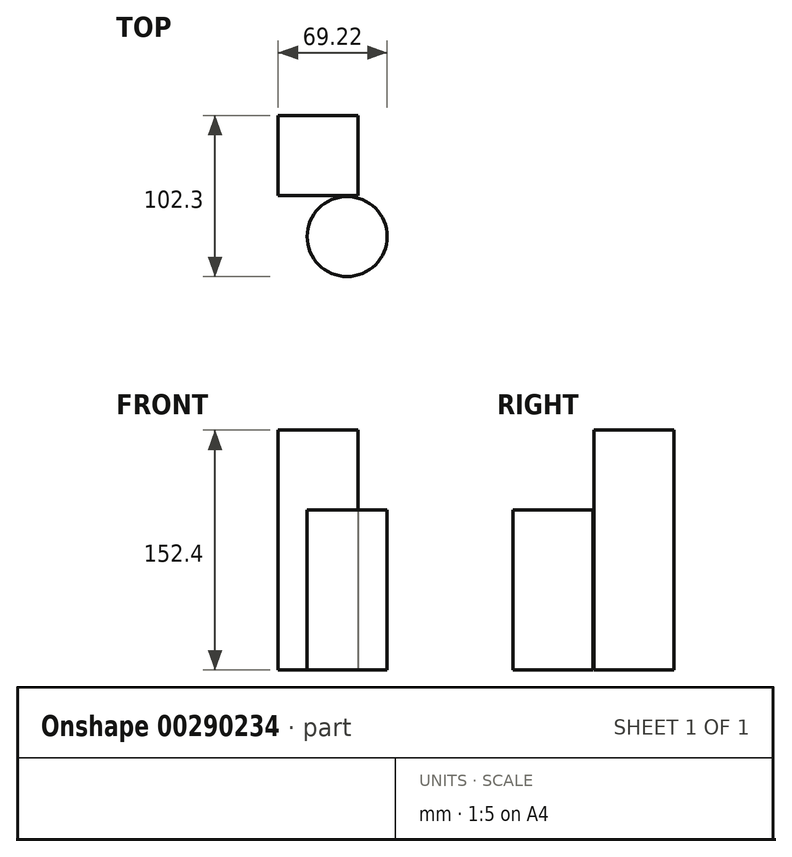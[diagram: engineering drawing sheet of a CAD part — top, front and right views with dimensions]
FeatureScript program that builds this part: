
annotation { "Feature Type Name" : "Feature", "Feature Type Description" : "" }
export const myFeature = defineFeature(function(context is Context, id is Id, definition is map)
    precondition{}
    {
        {
            var Q0;
            Q0=qCreatedBy(makeId("Top.planeOp"),FACE);
            var sketch = newSketch(context, id + "F0", { "sketchPlane" : qUnion([Q0])});
            skCircle(sketch, "E0", {"center": v(0, 0) * mm, "radius": 25.4 * mm});
            skSolve(sketch);
        }
        {
            var Q0;
            Q0=makeQuery(id+"F0.imprint","IMPRINT",FACE,{"disambiguationData":[TD([[makeQuery(id+"F0.imprint","IMPRINT",EDGE,{"derivedFrom":sQuery(id+"F0.wireOp",EDGE,"E0")}),1.0]])]});
            extrude(context, id + "F1", {"entities" : qUnion([Q0]), "depth" : 101.6 * mm});
        }
        {
            var Q0;
            Q0=qCreatedBy(makeId("Top.planeOp"),FACE);
            var sketch = newSketch(context, id + "F2", { "sketchPlane" : qUnion([Q0])});
            skLineSegment(sketch, "E1.bottom", {"start": v(6.98, 76.9) * mm, "end": v(-43.82, 76.9) * mm});
            skLineSegment(sketch, "E1.top", {"start": v(6.98, 26.1) * mm, "end": v(-43.82, 26.1) * mm});
            skLineSegment(sketch, "E1.left", {"start": v(6.98, 76.9) * mm, "end": v(6.98, 26.1) * mm});
            skLineSegment(sketch, "E1.right", {"start": v(-43.82, 76.9) * mm, "end": v(-43.82, 26.1) * mm});
            skPoint(sketch, "E1.middle", {"position": v(-18.42, 51.5) * mm});
            skSolve(sketch);
        }
        {
            var Q0;
            Q0 = qSketchRegion(id + "F2", true);
            extrude(context, id + "F3", {"entities" : qUnion([Q0]), "depth" : 152.4 * mm});
        }
    });
